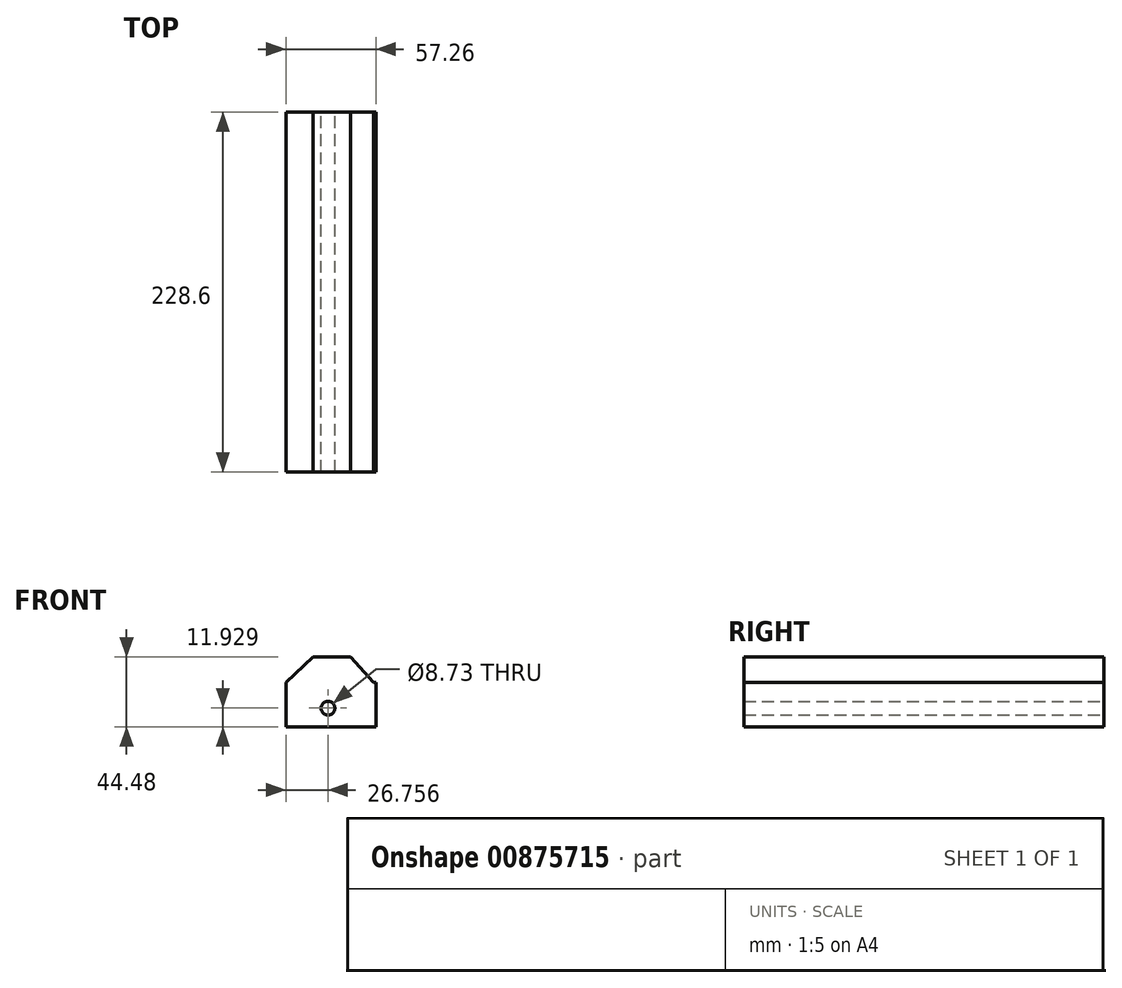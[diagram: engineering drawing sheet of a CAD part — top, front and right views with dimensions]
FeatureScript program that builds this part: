
annotation { "Feature Type Name" : "Feature", "Feature Type Description" : "" }
export const myFeature = defineFeature(function(context is Context, id is Id, definition is map)
    precondition{}
    {
        {
            var Q0;
            Q0=qCreatedBy(makeId("Front.planeOp"),FACE);
            var sketch = newSketch(context, id + "F0", { "sketchPlane" : qUnion([Q0])});
            skLineSegment(sketch, "E0.bottom", {"start": v(0, 0) * mm, "end": v(-57.26, 0) * mm});
            skLineSegment(sketch, "E0.top", {"start": v(0, 28.29) * mm, "end": v(-57.26, 28.29) * mm});
            skLineSegment(sketch, "E0.left", {"start": v(0, 0) * mm, "end": v(0, 28.29) * mm});
            skLineSegment(sketch, "E0.right", {"start": v(-57.26, 0) * mm, "end": v(-57.26, 28.29) * mm});
            skLineSegment(sketch, "E1", {"start": v(-57.26, 28.29) * mm, "end": v(-40.05, 44.48) * mm});
            skLineSegment(sketch, "E2", {"start": v(-40.05, 44.48) * mm, "end": v(-16.19, 44.48) * mm});
            skLineSegment(sketch, "E3", {"start": v(-16.19, 44.48) * mm, "end": v(-1.53, 28.29) * mm});
            skCircle(sketch, "E4", {"center": v(-30.5, 11.93) * mm, "radius": 4.36 * mm});
            skSolve(sketch);
        }
        {
            var Q0;
            Q0 = qSketchRegion(id + "F0", true);
            extrude(context, id + "F1", {"entities" : qUnion([Q0]), "depth" : 228.6 * mm, "offsetDistance" : 25.4 * mm});
        }
        {
            var Q0;
            Q0=makeQuery(id+"F1.opExtrude","SWEPT_FACE",FACE,{"disambiguationData":[OSD([sQuery(id+"F0.wireOp",EDGE,"E2")])]});
            var sketch = newSketch(context, id + "F2", { "sketchPlane" : qUnion([Q0])});
            skCircle(sketch, "E5", {"center": v(-31.02, -27.8) * mm, "radius": 4.12 * mm});
            skCircle(sketch, "E6", {"center": v(-31.02, -55.4) * mm, "radius": 7.19 * mm});
            skCircle(sketch, "E7", {"center": v(-28.97, -90.51) * mm, "radius": 4.64 * mm});
            skSolve(sketch);
        }
        {
            var Q0;
            Q0 = qSketchRegion(id + "F2", true);
            extrude(context, id + "F3", {"entities" : qUnion([Q0]), "operationType" : NewBodyOperationType.ADD, "depth" : -25.4 * mm, "offsetDistance" : 25.4 * mm});
        }
    });
